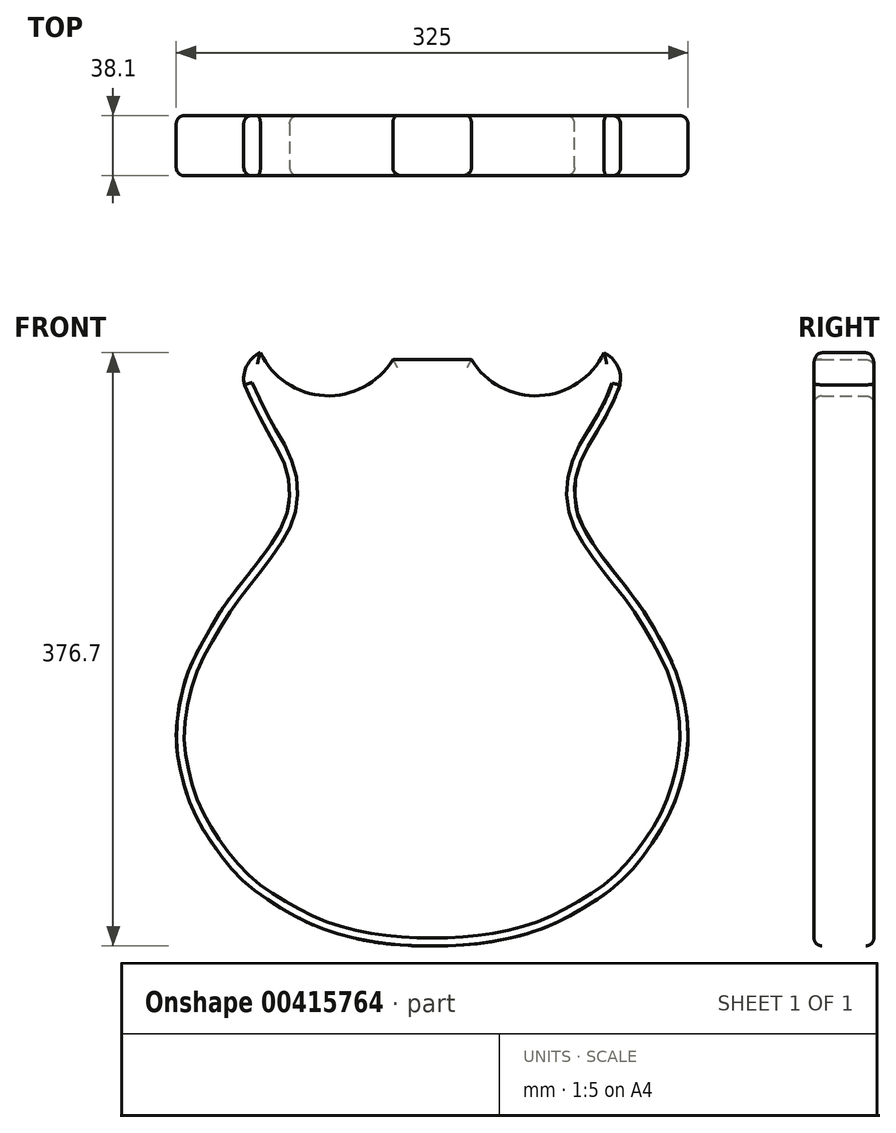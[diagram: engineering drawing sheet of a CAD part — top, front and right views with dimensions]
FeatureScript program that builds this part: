
annotation { "Feature Type Name" : "Feature", "Feature Type Description" : "" }
export const myFeature = defineFeature(function(context is Context, id is Id, definition is map)
    precondition{}
    {
        {
            var Q0;
            Q0=qCreatedBy(makeId("Front.planeOp"),FACE);
            var sketch = newSketch(context, id + "F0", { "sketchPlane" : qUnion([Q0])});
            skLineSegment(sketch, "E0", {"start": v(162.49, -189.9) * mm, "end": v(162.49, -358.78) * mm, "construction": true});
            skLineSegment(sketch, "E1", {"start": v(0, 94.7) * mm, "end": v(0, -358.78) * mm});
            skPoint(sketch, "E2", {"position": v(0, -323.19) * mm});
            skPoint(sketch, "E3", {"position": v(0, 50.52) * mm});
            skLineSegment(sketch, "E4", {"start": v(-162.49, -190.56) * mm, "end": v(162.49, -190.56) * mm});
            skFitSpline(sketch, "E5", {"points": [v(0, -321.82) * mm, v(19.28, -321.38) * mm, v(40.68, -318.7) * mm, v(61.02, -313.9) * mm, v(78.45, -307.27) * mm, v(90.42, -301) * mm, v(106.57, -291.18) * mm, v(122.53, -278.02) * mm, v(135.9, -262.16) * mm, v(147.05, -244.91) * mm, v(155.63, -226.16) * mm, v(161.07, -204.17) * mm, v(162.49, -190.56) * mm, v(161.19, -172.56) * mm, v(154.7, -147.38) * mm, v(143.17, -124.26) * mm, v(129.66, -102.6) * mm, v(108.68, -75.5) * mm, v(95.85, -55.88) * mm, v(92.07, -46.51) * mm, v(90.72, -38.14) * mm, v(90.73, -28.3) * mm, v(93.47, -16.5) * mm, v(97.6, -7.23) * mm, v(103.55, 2.84) * mm, v(119.16, 34.5) * mm], "startDerivative": vector(474.35, 0.52) * mm, "endDerivative": vector(77.75, 425.2) * mm});
            skFitSpline(sketch, "E6.MirrorCS", {"points": [v(0, -321.82) * mm, v(-19.29, -321.38) * mm, v(-40.68, -318.7) * mm, v(-61.02, -313.9) * mm, v(-78.44, -307.28) * mm, v(-90.44, -301) * mm, v(-106.58, -291.18) * mm, v(-122.53, -278.02) * mm, v(-135.91, -262.16) * mm, v(-147.06, -244.92) * mm, v(-155.64, -226.16) * mm, v(-161.07, -204.2) * mm, v(-162.48, -190.73) * mm, v(-161.18, -172.57) * mm, v(-154.7, -147.39) * mm, v(-143.17, -124.26) * mm, v(-129.66, -102.6) * mm, v(-108.68, -75.48) * mm, v(-95.84, -55.85) * mm, v(-92.09, -46.5) * mm, v(-90.74, -38.15) * mm, v(-90.74, -28.31) * mm, v(-93.5, -16.5) * mm, v(-97.61, -7.24) * mm, v(-103.53, 2.82) * mm, v(-119.16, 34.5) * mm], "startDerivative": vector(-474.35, 0.52) * mm, "endDerivative": vector(-169.26, 423.54) * mm});
            skLineSegment(sketch, "E7", {"start": v(0, 50.52) * mm, "end": v(24.96, 50.52) * mm});
            skLineSegment(sketch, "E8", {"start": v(0, 50.52) * mm, "end": v(-24.96, 50.52) * mm});
            skArc(sketch, "E9", {"start": v(119.16, 34.5) * mm, "mid": v(117.79, 46.52) * mm, "end": v(109.04, 54.88) * mm});
            skArc(sketch, "E10", {"start": v(24.96, 50.52) * mm, "mid": v(68.3, 27.6) * mm, "end": v(109.04, 54.88) * mm});
            skArc(sketch, "E11.MirrorCS", {"start": v(-24.96, 50.52) * mm, "mid": v(-68.3, 27.6) * mm, "end": v(-109.04, 54.88) * mm});
            skArc(sketch, "E12.MirrorCS", {"start": v(-119.16, 34.5) * mm, "mid": v(-117.79, 46.52) * mm, "end": v(-109.04, 54.88) * mm});
            skPoint(sketch, "E13", {"position": v(0, -115.06) * mm});
            skPoint(sketch, "E14", {"position": v(0, -95.8) * mm});
            skPoint(sketch, "E15", {"position": v(0, -20.03) * mm});
            skPoint(sketch, "E16", {"position": v(0, -0.88) * mm});
            skPoint(sketch, "E17", {"position": v(111.3, 16.24) * mm});
            skSolve(sketch);
        }
        {
            var Q0;
            {var subQ0=sQuery(id+"F0.wireOp",EDGE,"E8");Q0=makeQuery(id+"F0.imprint","IMPRINT",FACE,{"disambiguationData":[TD([[makeQuery(id+"F0.imprint","IMPRINT",EDGE,{"derivedFrom":subQ0}),1.0]])]});}
            var Q1;
            {var subQ0=sQuery(id+"F0.wireOp",EDGE,"E6.MirrorCS");var subQ3=sQuery(id+"F0.wireOp",EDGE,"E4");var subQ5=makeQuery(id+"F0.imprint","INTERSECT",VERTEX,{"derivedFrom":[subQ3,subQ0]});Q1=makeQuery(id+"F0.imprint","IMPRINT",FACE,{"disambiguationData":[TD([[makeQuery(id+"F0.imprint","IMPRINT",EDGE,{"disambiguationData":[TD([[subQ5,-1.0]])],"derivedFrom":subQ3}),-1.0]])]});}
            var Q2;
            {var subQ0=sQuery(id+"F0.wireOp",EDGE,"E5");var subQ3=sQuery(id+"F0.wireOp",EDGE,"E4");var subQ5=makeQuery(id+"F0.imprint","INTERSECT",VERTEX,{"derivedFrom":[subQ3,subQ0]});Q2=makeQuery(id+"F0.imprint","IMPRINT",FACE,{"disambiguationData":[TD([[makeQuery(id+"F0.imprint","IMPRINT",EDGE,{"disambiguationData":[TD([[subQ5,1.0]])],"derivedFrom":subQ3}),-1.0]])]});}
            var Q3;
            {var subQ0=sQuery(id+"F0.wireOp",EDGE,"E7");Q3=makeQuery(id+"F0.imprint","IMPRINT",FACE,{"disambiguationData":[TD([[makeQuery(id+"F0.imprint","IMPRINT",EDGE,{"derivedFrom":subQ0}),-1.0]])]});}
            extrude(context, id + "F1", {"entities" : qUnion([Q0, Q1, Q2, Q3]), "depth" : 38.1 * mm});
        }
        {
            var Q0;
            Q0=makeQuery(id+"F1.opExtrude","CAP_EDGE",EDGE,{"disambiguationData":[OSD([sQuery(id+"F0.wireOp",EDGE,"E6.MirrorCS")])],"isStart":false});
            var Q1;
            Q1=makeQuery(id+"F1.opExtrude","CAP_EDGE",EDGE,{"disambiguationData":[OSD([sQuery(id+"F0.wireOp",EDGE,"E5")])],"isStart":false});
            var Q2;
            Q2=makeQuery(id+"F1.opExtrude","CAP_EDGE",EDGE,{"disambiguationData":[OSD([sQuery(id+"F0.wireOp",EDGE,"E10")])],"isStart":false});
            var Q3;
            Q3=makeQuery(id+"F1.opExtrude","CAP_EDGE",EDGE,{"disambiguationData":[OSD([sQuery(id+"F0.wireOp",EDGE,"E11.MirrorCS")])],"isStart":false});
            var Q4;
            Q4=makeQuery(id+"F1.opExtrude","CAP_EDGE",EDGE,{"disambiguationData":[OSD([sQuery(id+"F0.wireOp",EDGE,"E9")])],"isStart":false});
            var Q5;
            Q5=makeQuery(id+"F1.opExtrude","CAP_EDGE",EDGE,{"disambiguationData":[OSD([sQuery(id+"F0.wireOp",EDGE,"E12.MirrorCS")])],"isStart":false});
            var Q6;
            Q6=makeQuery(id+"F1.opExtrude","CAP_EDGE",EDGE,{"disambiguationData":[OSD([sQuery(id+"F0.wireOp",EDGE,"E5")])],"isStart":true});
            var Q7;
            Q7=makeQuery(id+"F1.opExtrude","CAP_EDGE",EDGE,{"disambiguationData":[OSD([sQuery(id+"F0.wireOp",EDGE,"E6.MirrorCS")])],"isStart":true});
            var Q8;
            Q8=makeQuery(id+"F1.opExtrude","CAP_EDGE",EDGE,{"disambiguationData":[OSD([sQuery(id+"F0.wireOp",EDGE,"E12.MirrorCS")])],"isStart":true});
            var Q9;
            Q9=makeQuery(id+"F1.opExtrude","CAP_EDGE",EDGE,{"disambiguationData":[OSD([sQuery(id+"F0.wireOp",EDGE,"E11.MirrorCS")])],"isStart":true});
            var Q10;
            Q10=makeQuery(id+"F1.opExtrude","CAP_EDGE",EDGE,{"disambiguationData":[OSD([sQuery(id+"F0.wireOp",EDGE,"E7"),sQuery(id+"F0.wireOp",EDGE,"E8")])],"isStart":true});
            var Q11;
            Q11=makeQuery(id+"F1.opExtrude","CAP_EDGE",EDGE,{"disambiguationData":[OSD([sQuery(id+"F0.wireOp",EDGE,"E10")])],"isStart":true});
            var Q12;
            Q12=makeQuery(id+"F1.opExtrude","CAP_EDGE",EDGE,{"disambiguationData":[OSD([sQuery(id+"F0.wireOp",EDGE,"E9")])],"isStart":true});
            fillet(context, id + "F2", {"entities" : qUnion([Q0, Q1, Q2, Q3, Q4, Q5, Q6, Q7, Q8, Q9, Q10, Q11, Q12]), "radius" : 5.08 * mm, "tangentPropagation" : true, "allowEdgeOverflow" : false});
        }
    });
